# Revit family: PlumFix_Bath_ABEY_Patinato_Petite ClearStone_1524mm_Face Based
name_source: partatom
category: Plumbing Fixtures
revit_build: Autodesk Revit 2016 (Build: 20150220_1215(x64)
units: mm (PartAtom-declared; Revit-internal decimal feet)

## family parameters
Cut with Voids When Loaded = Yes
Host = Face
OmniClass Number = 23.45.05.14.21
OmniClass Title = Bathtubs
Part Type = Normal
Room Calculation Point = No
Round Connector Dimension = Use Diameter
Shared = No

## types (1)
- 1524w x 800d x 550h
    Assembly Code = 0.00
    BodyMaterial = z_Abey_White Stone
    CW Connection = No
    Default Elevation = 0 mm  [stored 0 ft]
    Description = Patinato - Petite 1524mm ClearStone Bath - White Stone
    HW Connection = No
    Manufacturer = Abey Australia
    Manufacturer_Overall Depth = 800 mm  [stored 2.62467 ft]
    Manufacturer_Overall Height = 550 mm  [stored 1.80446 ft]
    Manufacturer_Overall Width = 1524 mm  [stored 5 ft]
    Manufacturer_Spec Code = 22829
    Manufacturer_URL__Product Specific = https://www.abey.com.au
    Model = 22829
    ModifiedIssue_ANZRS = 20190823 $
    Type Comments = 1524w
    URL = https://www.abey.com.au
    Vent Connection = No
    Waste Connection = Yes

note: [stored X ft] marks values corroborated as IEEE doubles in the binary element streams (Revit-internal decimal feet)

## geometry (parser evidence)
native form markers: Sweep x8
no freeform markers — native parametric forms only
